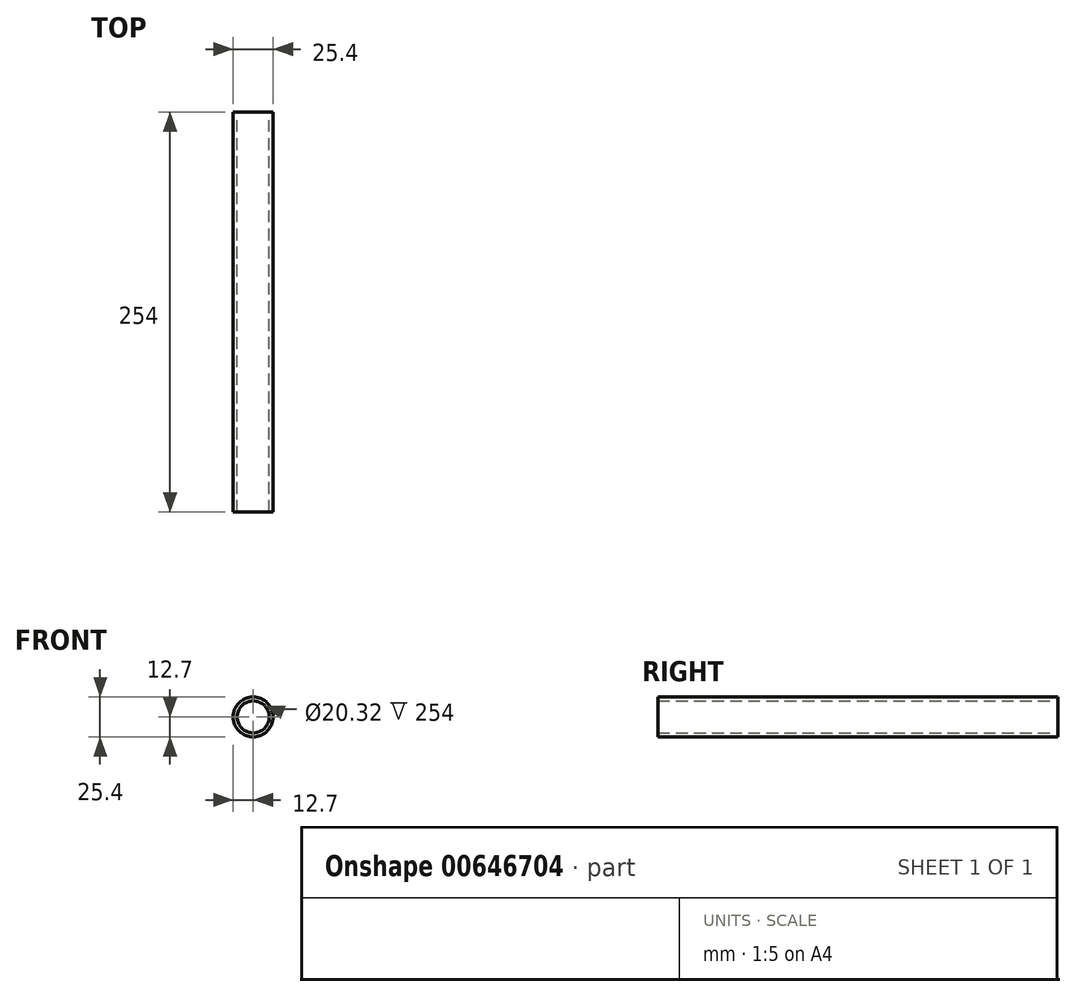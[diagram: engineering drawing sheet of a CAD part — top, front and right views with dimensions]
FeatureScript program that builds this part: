
annotation { "Feature Type Name" : "Feature", "Feature Type Description" : "" }
export const myFeature = defineFeature(function(context is Context, id is Id, definition is map)
    precondition{}
    {
        {
            var Q0;
            Q0=qCreatedBy(makeId("Front.planeOp"),FACE);
            var sketch = newSketch(context, id + "F0", { "sketchPlane" : qUnion([Q0])});
            skCircle(sketch, "E0", {"center": v(0, 0) * mm, "radius": 12.7 * mm});
            skCircle(sketch, "E1", {"center": v(0, 0) * mm, "radius": 10.16 * mm});
            skSolve(sketch);
        }
        {
            var Q0;
            Q0=makeQuery(id+"F0.imprint","IMPRINT",FACE,{"disambiguationData":[TD([[makeQuery(id+"F0.imprint","IMPRINT",EDGE,{"derivedFrom":sQuery(id+"F0.wireOp",EDGE,"E0")}),1.0]])]});
            extrude(context, id + "F1", {"entities" : qUnion([Q0]), "depth" : 254 * mm, "offsetDistance" : 25.4 * mm});
        }
    });
